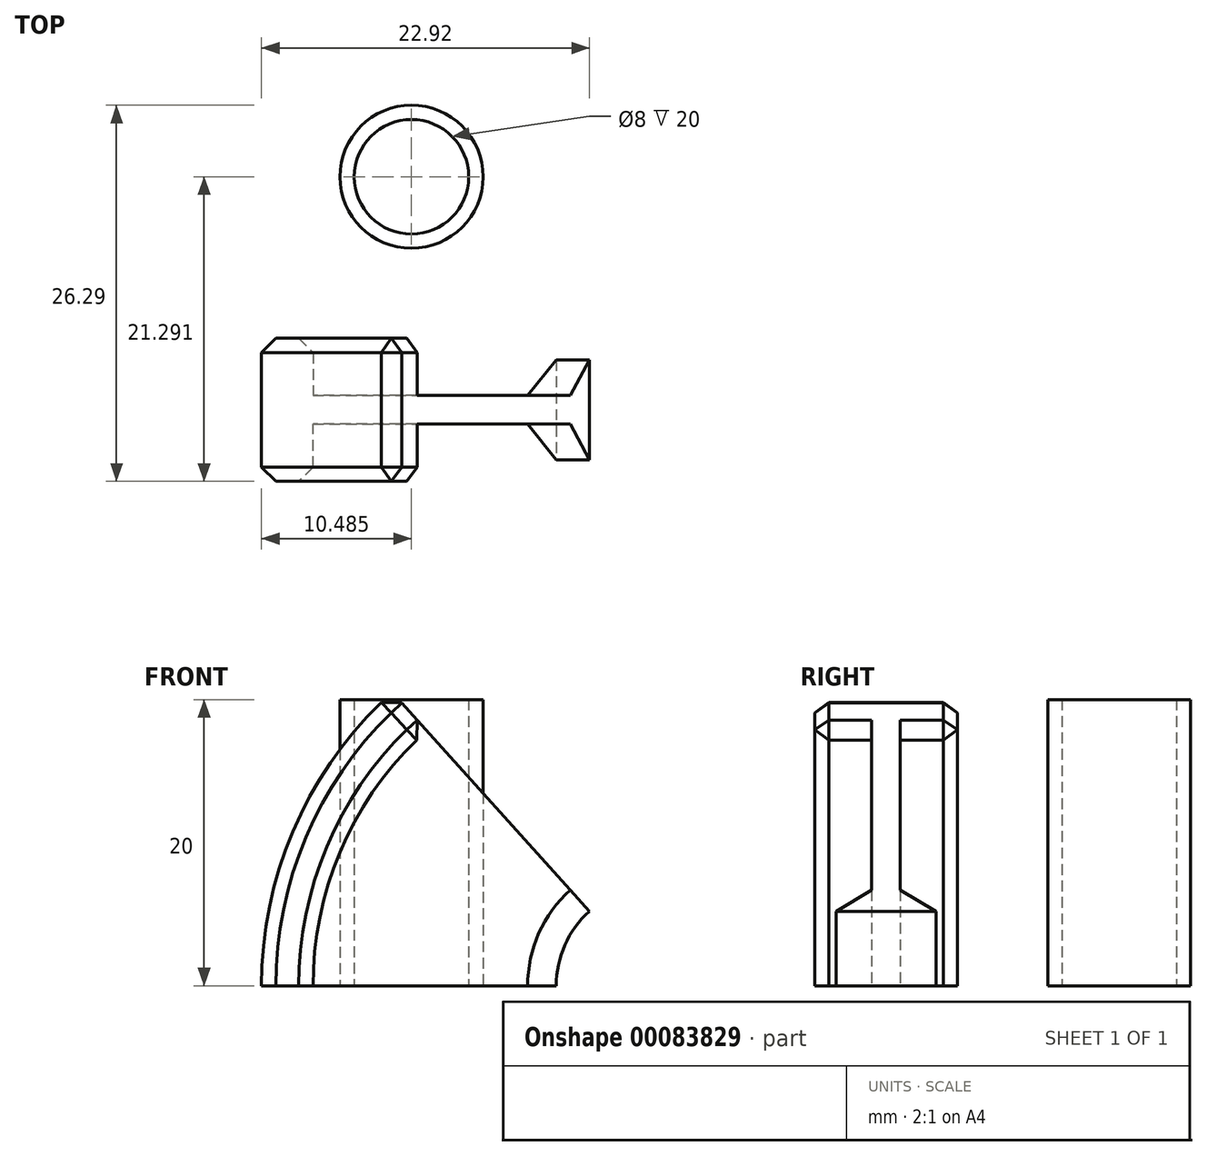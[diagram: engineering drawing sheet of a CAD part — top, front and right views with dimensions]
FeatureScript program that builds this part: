
annotation { "Feature Type Name" : "Feature", "Feature Type Description" : "" }
export const myFeature = defineFeature(function(context is Context, id is Id, definition is map)
    precondition{}
    {
        {
            var Q0;
            Q0=qCreatedBy(makeId("Top.planeOp"),FACE);
            var sketch = newSketch(context, id + "F0", { "sketchPlane" : qUnion([Q0])});
            skLineSegment(sketch, "E0", {"start": v(-24.6, 5) * mm, "end": v(-21, 5) * mm});
            skLineSegment(sketch, "E1", {"start": v(-21, 5) * mm, "end": v(-21, 1) * mm});
            skLineSegment(sketch, "E2", {"start": v(-21, 1) * mm, "end": v(-6, 1) * mm});
            skLineSegment(sketch, "E3", {"start": v(-6, 1) * mm, "end": v(-4, 3.48) * mm});
            skLineSegment(sketch, "E4", {"start": v(-24.6, 5) * mm, "end": v(-24.6, -5) * mm});
            skLineSegment(sketch, "E5.MirrorCS", {"start": v(-24.6, -5) * mm, "end": v(-21, -5) * mm});
            skLineSegment(sketch, "E6.MirrorCS", {"start": v(-21, -5) * mm, "end": v(-21, -1) * mm});
            skLineSegment(sketch, "E7.MirrorCS", {"start": v(-21, -1) * mm, "end": v(-6, -1) * mm});
            skLineSegment(sketch, "E8.MirrorCS", {"start": v(-6, -1) * mm, "end": v(-4, -3.48) * mm});
            skLineSegment(sketch, "E9", {"start": v(-4, 3.48) * mm, "end": v(-4, -3.48) * mm});
            skLineSegment(sketch, "E10", {"start": v(3, 3.95) * mm, "end": v(3, -3.35) * mm});
            skSolve(sketch);
        }
        {
            var Q0;
            Q0 = qSketchRegion(id + "F0", true);
            var Q1;
            Q1=sQuery(id+"F0.wireOp",EDGE,"E10");
            revolve(context, id + "F1", {"entities" : qUnion([Q0]), "axis" : qUnion([Q1]), "revolveType" : RevolveType.ONE_DIRECTION, "oppositeDirection" : true, "angle" : 48 * degree});
        }
        {
            var Q0;
            Q0=makeQuery(id+"F1.opRevolve","CAP_EDGE",EDGE,{"disambiguationData":[OSD([sQuery(id+"F0.wireOp",EDGE,"E4")])],"isStart":false});
            var Q1;
            Q1=makeQuery(id+"F1.opRevolve","CAP_EDGE",EDGE,{"disambiguationData":[OSD([sQuery(id+"F0.wireOp",EDGE,"E5.MirrorCS")])],"isStart":false});
            var Q2;
            Q2=makeQuery(id+"F1.opRevolve","CAP_EDGE",EDGE,{"disambiguationData":[OSD([sQuery(id+"F0.wireOp",EDGE,"E0")])],"isStart":false});
            var Q3;
            Q3=makeQuery(id+"F1.opRevolve","CAP_EDGE",EDGE,{"disambiguationData":[OSD([sQuery(id+"F0.wireOp",EDGE,"E6.MirrorCS")])],"isStart":false});
            var Q4;
            Q4=makeQuery(id+"F1.opRevolve","CAP_EDGE",EDGE,{"disambiguationData":[OSD([sQuery(id+"F0.wireOp",EDGE,"E1")])],"isStart":false});
            var Q5;
            Q5=makeQuery(id+"F1.opRevolve","SWEPT_EDGE",EDGE,{"disambiguationData":[OSD([sQuery(id+"F0.wireOp",EDGE,"E4"),sQuery(id+"F0.wireOp",EDGE,"E5.MirrorCS")])]});
            var Q6;
            Q6=makeQuery(id+"F1.opRevolve","SWEPT_EDGE",EDGE,{"disambiguationData":[OSD([sQuery(id+"F0.wireOp",EDGE,"E5.MirrorCS"),sQuery(id+"F0.wireOp",EDGE,"E6.MirrorCS")])]});
            var Q7;
            Q7=makeQuery(id+"F1.opRevolve","SWEPT_EDGE",EDGE,{"disambiguationData":[OSD([sQuery(id+"F0.wireOp",EDGE,"E0"),sQuery(id+"F0.wireOp",EDGE,"E4")])]});
            var Q8;
            Q8=makeQuery(id+"F1.opRevolve","SWEPT_EDGE",EDGE,{"disambiguationData":[OSD([sQuery(id+"F0.wireOp",EDGE,"E0"),sQuery(id+"F0.wireOp",EDGE,"E1")])]});
            chamfer(context, id + "F2", {"entities" : qUnion([Q0, Q1, Q2, Q3, Q4, Q5, Q6, Q7, Q8]), "width" : 1 * mm, "tangentPropagation" : true});
        }
        {
            var Q0;
            Q0=qCreatedBy(makeId("Top.planeOp"),FACE);
            var sketch = newSketch(context, id + "F3", { "sketchPlane" : qUnion([Q0])});
            skCircle(sketch, "E11", {"center": v(-14.11, 16.3) * mm, "radius": 5 * mm});
            skCircle(sketch, "E12", {"center": v(-14.11, 16.3) * mm, "radius": 4 * mm});
            skSolve(sketch);
        }
        {
            var Q0;
            Q0 = qSketchRegion(id + "F3", true);
            extrude(context, id + "F4", {"entities" : qUnion([Q0]), "depth" : 20 * mm});
        }
    });
